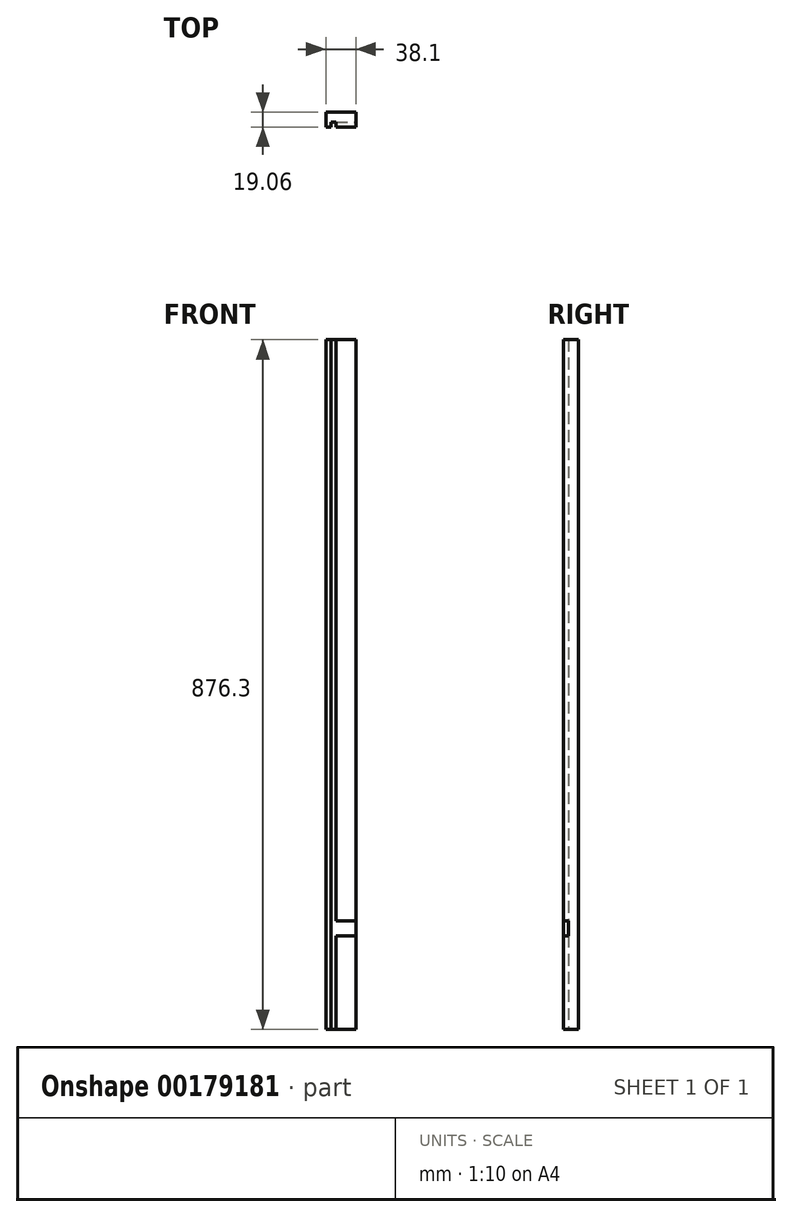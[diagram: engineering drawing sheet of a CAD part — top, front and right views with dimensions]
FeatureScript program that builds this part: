
annotation { "Feature Type Name" : "Feature", "Feature Type Description" : "" }
export const myFeature = defineFeature(function(context is Context, id is Id, definition is map)
    precondition{}
    {
        {
            var Q0;
            Q0=qCreatedBy(makeId("Front.planeOp"),FACE);
            var sketch = newSketch(context, id + "F0", { "sketchPlane" : qUnion([Q0])});
            skLineSegment(sketch, "E0.bottom", {"start": v(-32, 438.15) * mm, "end": v(6.1, 438.15) * mm});
            skLineSegment(sketch, "E0.top", {"start": v(-32, -438.15) * mm, "end": v(6.1, -438.15) * mm});
            skLineSegment(sketch, "E0.left", {"start": v(-32, 438.15) * mm, "end": v(-32, -438.15) * mm});
            skLineSegment(sketch, "E0.right", {"start": v(6.1, 438.15) * mm, "end": v(6.1, -438.15) * mm});
            skLineSegment(sketch, "E1", {"start": v(-32, 0) * mm, "end": v(6.1, 0) * mm});
            skSolve(sketch);
        }
        {
            var Q0;
            {var subQ0=sQuery(id+"F0.wireOp",EDGE,"E0.bottom");Q0=makeQuery(id+"F0.imprint","IMPRINT",FACE,{"disambiguationData":[TD([[makeQuery(id+"F0.imprint","IMPRINT",EDGE,{"derivedFrom":subQ0}),-1.0]])]});}
            var Q1;
            {var subQ0=sQuery(id+"F0.wireOp",EDGE,"E0.top");Q1=makeQuery(id+"F0.imprint","IMPRINT",FACE,{"disambiguationData":[TD([[makeQuery(id+"F0.imprint","IMPRINT",EDGE,{"derivedFrom":subQ0}),1.0]])]});}
            extrude(context, id + "F1", {"entities" : qUnion([Q0, Q1]), "depth" : 19.05 * mm, "symmetric" : true});
        }
        {
            var Q0;
            Q0=makeQuery(id+"F1.opExtrude","CAP_FACE",FACE,{"disambiguationData":[OSD([sQuery(id+"F0.wireOp",EDGE,"E0.bottom"),sQuery(id+"F0.wireOp",EDGE,"E0.top"),sQuery(id+"F0.wireOp",EDGE,"E0.left"),sQuery(id+"F0.wireOp",EDGE,"E0.right")])],"isStart":false});
            var sketch = newSketch(context, id + "F2", { "sketchPlane" : qUnion([Q0])});
            skLineSegment(sketch, "E2.bottom", {"start": v(-25.65, 438.15) * mm, "end": v(-19.3, 438.15) * mm});
            skLineSegment(sketch, "E2.top", {"start": v(-25.65, -438.15) * mm, "end": v(-19.3, -438.15) * mm});
            skLineSegment(sketch, "E2.left", {"start": v(-25.65, 438.15) * mm, "end": v(-25.65, -438.15) * mm});
            skLineSegment(sketch, "E2.right", {"start": v(-19.3, 438.15) * mm, "end": v(-19.3, -438.15) * mm});
            skSolve(sketch);
        }
        {
            var Q0;
            Q0=makeQuery(id+"F2.imprint","IMPRINT",FACE,{"disambiguationData":[TD([[makeQuery(id+"F2.imprint","IMPRINT",EDGE,{"derivedFrom":sQuery(id+"F2.wireOp",EDGE,"E2.bottom")}),-1.0]])]});
            extrude(context, id + "F3", {"entities" : qUnion([Q0]), "operationType" : NewBodyOperationType.REMOVE, "oppositeDirection" : true, "depth" : 6.35 * mm});
        }
        {
            var Q0;
            {var subQ0=sQuery(id+"F0.wireOp",EDGE,"E0.bottom");var subQ1=sQuery(id+"F0.wireOp",EDGE,"E0.top");var subQ2=sQuery(id+"F0.wireOp",EDGE,"E0.right");Q0=makeQuery(id+"F3.boolean.opBoolean","SPLIT",FACE,{"disambiguationData":[TD([makeQuery(id+"F1.opExtrude","SWEPT_FACE",FACE,{"disambiguationData":[OSD([subQ2])]})])],"derivedFrom":makeQuery(id+"F1.opExtrude","CAP_FACE",FACE,{"disambiguationData":[OSD([subQ0,subQ1,sQuery(id+"F0.wireOp",EDGE,"E0.left"),subQ2])],"isStart":false})});}
            var sketch = newSketch(context, id + "F4", { "sketchPlane" : qUnion([Q0])});
            skLineSegment(sketch, "E3.bottom", {"start": v(-19.3, -319.09) * mm, "end": v(6.1, -319.09) * mm});
            skLineSegment(sketch, "E3.top", {"start": v(-19.3, -300.04) * mm, "end": v(6.1, -300.04) * mm});
            skLineSegment(sketch, "E3.left", {"start": v(-19.3, -319.09) * mm, "end": v(-19.3, -300.04) * mm});
            skLineSegment(sketch, "E3.right", {"start": v(6.1, -319.09) * mm, "end": v(6.1, -300.04) * mm});
            skSolve(sketch);
        }
        {
            var Q0;
            Q0=makeQuery(id+"F4.imprint","IMPRINT",FACE,{"disambiguationData":[TD([[makeQuery(id+"F4.imprint","IMPRINT",EDGE,{"derivedFrom":sQuery(id+"F4.wireOp",EDGE,"E3.bottom")}),1.0]])]});
            extrude(context, id + "F5", {"entities" : qUnion([Q0]), "operationType" : NewBodyOperationType.REMOVE, "oppositeDirection" : true, "depth" : 6.35 * mm});
        }
    });
